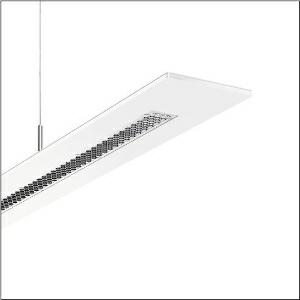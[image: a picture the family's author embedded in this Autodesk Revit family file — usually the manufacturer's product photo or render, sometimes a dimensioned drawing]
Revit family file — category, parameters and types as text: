
# Revit family: arktika_r__21_duo_5mb252dl60840_f6f7
name_source: partatom
category: Lighting Fixtures
units: mm (PartAtom-declared; Revit-internal decimal feet)

## family parameters
Cut with Voids When Loaded = No
Host = Face
Light Source = No
Part Type = Normal
Room Calculation Point = No
Round Connector Dimension = Use Diameter
Shared = No

## types (1)
- --- (1 x LED 4000K / CRI = 80 (unbekannt), 8800 lm, 4000K)
    Apparent Load = 67 VA
    CIE Flux Codes = 81 100 100 79 100
    Color Rendering = 80
    Color Temperature = 4000K
    Default Elevation = 1800 mm
    Description = Arktika® 21 duo, office luminaire, primary anti-glare with honeycomb louvre, of plastic, aluminium vaporised, highly specular, light emission: direct/indirect distribution, primary light characteristic: symmetric, installation type: suspended mounting, LED, rated luminous flux: 8.800lm, luminous efficacy: 132lm/W, light colour: 840, colour temperature: 4000K, control gear: DALI, with terminal, 3+2-pole, max. 2.5mm², mains connection: 220..240V, AC, 50/60Hz, rated input power: 67W, housing, of aluminium, powder-coated, traffic white (RAL 9016), 2-length, length: 2.280mm, width: 120mm, height: 8mm, protection rating (complete): IP20, insulation class (complete): insulation class II (safety insulation), certification: CE, packaging unit: 1 piece
    Height = 8 mm  [stored 0.0262467 ft]
    Lamp = 1 x LED 4000K / CRI >= 80 (unbekannt)
    Lamp Light Flux = 8800 lm
    Lamp count = 1
    Length = 2280 mm
    Luminous efficacy = 132 lm/W
    Manufacturer = Siteco
    ModVariant = No
    Model = 5MB252DL60840
    Mounting Place = Ceiling
    Mounting Type = Pendant
    Number of Poles = 1
    OnlyDefault = Yes
    Power Factor = 1
    Product Name = Arktika® 21 duo
    Product group = office luminaire | ceiling pendant
    ProductGroupID = 903
    Protection Class = Protection class II
    Protection Degree = IP 20
    RLX_Detail_Level = 1
    RLX_Emergency_Light_Flux = 0 lm
    RLX_Emergency_Type = 0
    RLX_Emergency_Type_DB = No
    RlxData = <blob elided: 39821 chars, md5=230e3af7>
    Socket = socket
    Standby Power = 0 W
    System Light Flux = 8800 lm
    System Power = 67 W
    Type Comments = factory setting: luminous flux: 100 % | dim-lin: 254 | 1330 mA
    Type Image = l_1006128.jpg
    URL = http://relux.com
    VarID = @adj_219825
    Voltage = 0 V
    Weight = 0.00 kg
    Width = 120 mm

note: [stored X ft] marks values corroborated as IEEE doubles in the binary element streams (Revit-internal decimal feet)

## geometry (parser evidence)
native form markers: Blend x4, Sweep x12
no freeform markers — native parametric forms only
